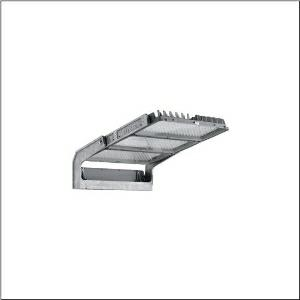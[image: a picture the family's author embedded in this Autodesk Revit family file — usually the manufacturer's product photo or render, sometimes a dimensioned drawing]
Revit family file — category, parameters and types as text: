
# Revit family: floodlight_fl_11_maxi_pro___rs07_5xa779129k02fb_e546
name_source: partatom
category: Lighting Fixtures
units: mm (PartAtom-declared; Revit-internal decimal feet)

## family parameters
Cut with Voids When Loaded = No
Host = Face
Light Source = No
Part Type = Normal
Room Calculation Point = No
Round Connector Dimension = Use Diameter
Shared = No

## types (1)
- --- (1 x LED, 173450 lm, 1400 W, 5700K)
    Apparent Load = 1400 VA
    CIE Flux Codes = 80 93 99 100 99
    Color Rendering = 70
    Color Temperature = 5700K
    Default Elevation = 1800 mm
    Description = Floodlight FL 11  maxi  pro floodlight; light control with lens of PMMA; cover panel of toughened safety glass, transparent; light distribution: RS07, rotationally symmetric direct distribution, LEDcolour temperature: 5700K, rated luminous flux: 173.450lm, colour rendering: CRI > 70, light colour: 757; luminous efficacy: 124lm/W; brightness control: DALI 2; with terminal, 5-pole, max. 2.5mm², mains connection: 220..240V/380..400V AC, 50/60Hz, surge voltage resistance: line to ground: 10kV, service life up to 100,000h L90. Typical operating time: 1000h per year, ECG replaceable separately, LED unit replaceable without ESD environment, dustproof LED module, dimming range 10..100%; 1400W floodlight with 3x LED unit of diecast aluminium, coated grey; length: 1.003mm / width: 651mm / height: 338mm; mounting bracket, of diecast aluminium, uncoated, natural, protection rating (complete): IP66; insulation class (complete): insulation class I (protective earthing); certification: CE, ENEC, VDE; ball protection: ball impact resistant, only for outdoor installations in the designated locations, permissible operating ambient temperature: -45..+55°C, permissible storage temperature: -40..+85°Cpackaging unit: 1 piece

Light Distribution: RS07
    Height = 320 mm
    Lamp = 1 x LED
    Lamp Light Flux = 173450 lm
    Lamp Power = 1400 W
    Lamp count = 1
    Length = 1002 mm
    Luminous efficacy = 124 lm/W
    Manufacturer = Siteco
    ModVariant = No
    Model = 5XA779129K02FB
    Mounting Place = Ceiling
    Mounting Type = Surface mounted
    Number of Poles = 1
    OnlyDefault = Yes
    Power Factor = 1
    Product Name = Floodlight FL 11 maxi pro | RS07
    Product group = floodlight | ceiling mounted
    ProductGroupID = 301
    Protection Class = Protection class I
    Protection Degree = IP 66
    RLX_Detail_Level = 1
    RLX_Emergency_Light_Flux = 0 lm
    RLX_Emergency_Type = 0
    RLX_Emergency_Type_DB = No
    RlxData = <blob elided: 40413 chars, md5=136a50c3>
    Socket = socket
    Standby Power = 0 W
    System Light Flux = 173450 lm
    System Power = 1400 W
    Type Comments = factory setting: luminous flux: 100 % | dim-lin: 254 | 955 mA
    Type Image = l_1356210.jpg
    URL = http://relux.com
    VarID = @adj_023542
    Voltage = 0 V
    Weight = 0.00 kg
    Width = 655 mm

## geometry (parser evidence)
native form markers: Blend x4, Sweep x13
no freeform markers — native parametric forms only
